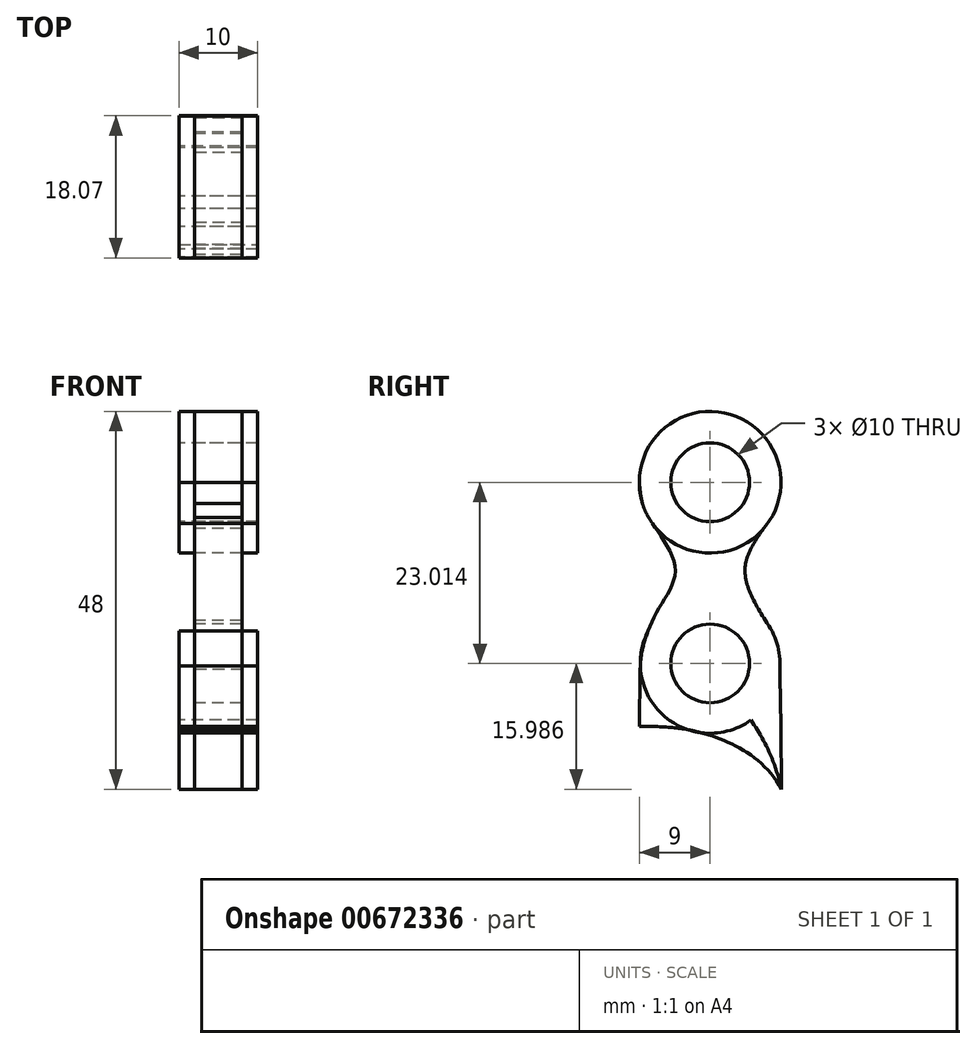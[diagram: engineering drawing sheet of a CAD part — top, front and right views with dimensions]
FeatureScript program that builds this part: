
annotation { "Feature Type Name" : "Feature", "Feature Type Description" : "" }
export const myFeature = defineFeature(function(context is Context, id is Id, definition is map)
    precondition{}
    {
        {
            var Q0;
            Q0=qCreatedBy(makeId("Right.planeOp"),FACE);
            var sketch = newSketch(context, id + "F0", { "sketchPlane" : qUnion([Q0])});
            skLineSegment(sketch, "E0.bottom", {"start": v(0, 20) * mm, "end": v(0, 20) * mm});
            skPoint(sketch, "E0.middle", {"position": v(0, 0) * mm});
            skFitSpline(sketch, "E1", {"points": [v(-9, -20) * mm, v(0, -21.15) * mm, v(9.07, -28) * mm], "startDerivative": vector(21.95, 0) * mm, "endDerivative": vector(11.4, -21.33) * mm});
            skFitSpline(sketch, "E2", {"points": [v(9.07, -28) * mm, v(9, -20) * mm], "startDerivative": vector(-0.05, 5.73) * mm, "endDerivative": vector(-0.05, 5.73) * mm});
            skPoint(sketch, "E3.visualSharp", {"position": v(9, 20) * mm});
            skArc(sketch, "E3.filletArc", {"start": v(9, 11) * mm, "mid": v(6.36, 17.36) * mm, "end": v(0, 20) * mm});
            skPoint(sketch, "E4.visualSharp", {"position": v(-9, 20) * mm});
            skArc(sketch, "E4.filletArc", {"start": v(0, 20) * mm, "mid": v(-6.36, 17.36) * mm, "end": v(-9, 11) * mm});
            skCircle(sketch, "E5", {"center": v(0, 11) * mm, "radius": 9 * mm});
            skCircle(sketch, "E6.0", {"center": v(0, 11) * mm, "radius": 5 * mm});
            skFitSpline(sketch, "E7.MirrorCS", {"points": [v(-9, -20) * mm, v(-8.54, -10) * mm, v(-6.66, -5.3) * mm, v(-4.43, 0) * mm, v(-7.33, 5.78) * mm, v(-8.59, 8.3) * mm, v(-9, 11) * mm], "startDerivative": vector(1.82, 96.63) * mm, "endDerivative": vector(-2.09, 21.27) * mm});
            skCircle(sketch, "E8", {"center": v(0, -12.01) * mm, "radius": 8.88 * mm});
            skCircle(sketch, "E9", {"center": v(0, -12.01) * mm, "radius": 5 * mm});
            skFitSpline(sketch, "E10", {"points": [v(4.43, 0) * mm, v(0, -12.01) * mm, v(9.07, -28) * mm], "startDerivative": vector(-11.72, -51.29) * mm, "endDerivative": vector(11.05, -50.26) * mm});
            skFitSpline(sketch, "E11", {"points": [v(4.43, 0) * mm, v(0, 11) * mm], "startDerivative": vector(-13.3, 18) * mm, "endDerivative": vector(-10.3, 15) * mm});
            skFitSpline(sketch, "E12", {"points": [v(7.6, 6.18) * mm, v(4.43, 0) * mm, v(7, -6.56) * mm], "startDerivative": vector(-9.2, -12.26) * mm, "endDerivative": vector(8.03, -13.2) * mm});
            skFitSpline(sketch, "E13", {"points": [v(9, -20) * mm, v(8.81, -10.96) * mm], "startDerivative": vector(-0.17, 9.05) * mm, "endDerivative": vector(-0.17, 9.05) * mm});
            skSolve(sketch);
        }
        {
            var Q0;
            {var subQ0=sQuery(id+"F0.wireOp",EDGE,"E7.MirrorCS");var subQ1=sQuery(id+"F0.wireOp",EDGE,"E1");var subQ2=makeQuery(id+"F0.imprint","INTERSECT",VERTEX,{"derivedFrom":[subQ1,subQ0]});Q0=makeQuery(id+"F0.imprint","IMPRINT",FACE,{"disambiguationData":[TD([[makeQuery(id+"F0.imprint","IMPRINT",EDGE,{"disambiguationData":[TD([[subQ2,-1.0]])],"derivedFrom":subQ1}),1.0]])]});}
            var Q1;
            {var subQ0=sQuery(id+"F0.wireOp",EDGE,"E8");var subQ1=sQuery(id+"F0.wireOp",EDGE,"E1");var subQ2=makeQuery(id+"F0.imprint","INTERSECT",VERTEX,{"disambiguationData":[OD(0.0)],"derivedFrom":[subQ1,subQ0]});Q1=makeQuery(id+"F0.imprint","IMPRINT",FACE,{"disambiguationData":[TD([[makeQuery(id+"F0.imprint","IMPRINT",EDGE,{"disambiguationData":[TD([[subQ2,-1.0]])],"derivedFrom":subQ1}),-1.0]])]});}
            var Q2;
            {var subQ0=sQuery(id+"F0.wireOp",EDGE,"E10");var subQ1=sQuery(id+"F0.wireOp",EDGE,"E1");var subQ2=makeQuery(id+"F0.imprint","INTERSECT",VERTEX,{"derivedFrom":[subQ1,subQ0]});Q2=makeQuery(id+"F0.imprint","IMPRINT",FACE,{"disambiguationData":[TD([[makeQuery(id+"F0.imprint","IMPRINT",EDGE,{"disambiguationData":[TD([[subQ2,1.0]])],"derivedFrom":subQ1}),1.0]])]});}
            var Q3;
            {var subQ0=sQuery(id+"F0.wireOp",EDGE,"E7.MirrorCS");var subQ1=sQuery(id+"F0.wireOp",EDGE,"E5");var subQ2=makeQuery(id+"F0.imprint","INTERSECT",VERTEX,{"disambiguationData":[OD(0.0)],"derivedFrom":[subQ1,subQ0]});Q3=makeQuery(id+"F0.imprint","IMPRINT",FACE,{"disambiguationData":[TD([[makeQuery(id+"F0.imprint","IMPRINT",EDGE,{"disambiguationData":[TD([[subQ2,-1.0]])],"derivedFrom":subQ1}),1.0]])]});}
            var Q4;
            {var subQ0=sQuery(id+"F0.wireOp",EDGE,"E7.MirrorCS");var subQ1=sQuery(id+"F0.wireOp",EDGE,"E5");var subQ2=makeQuery(id+"F0.imprint","INTERSECT",VERTEX,{"disambiguationData":[OD(1.0)],"derivedFrom":[subQ1,subQ0]});Q4=makeQuery(id+"F0.imprint","IMPRINT",FACE,{"disambiguationData":[TD([[makeQuery(id+"F0.imprint","IMPRINT",EDGE,{"disambiguationData":[TD([[subQ2,-1.0]])],"derivedFrom":subQ1}),-1.0]])]});}
            var Q5;
            {var subQ0=sQuery(id+"F0.wireOp",EDGE,"E7.MirrorCS");var subQ1=sQuery(id+"F0.wireOp",EDGE,"E5");var subQ2=makeQuery(id+"F0.imprint","INTERSECT",VERTEX,{"disambiguationData":[OD(2.0)],"derivedFrom":[subQ1,subQ0]});Q5=makeQuery(id+"F0.imprint","IMPRINT",FACE,{"disambiguationData":[TD([[makeQuery(id+"F0.imprint","IMPRINT",EDGE,{"disambiguationData":[TD([[subQ2,-1.0]])],"derivedFrom":subQ1}),1.0]])]});}
            var Q6;
            {var subQ0=sQuery(id+"F0.wireOp",EDGE,"E12");var subQ1=sQuery(id+"F0.wireOp",EDGE,"E5");var subQ2=makeQuery(id+"F0.imprint","INTERSECT",VERTEX,{"disambiguationData":[OD(0.0)],"derivedFrom":[subQ1,subQ0]});Q6=makeQuery(id+"F0.imprint","IMPRINT",FACE,{"disambiguationData":[TD([[makeQuery(id+"F0.imprint","IMPRINT",EDGE,{"disambiguationData":[TD([[subQ2,1.0]])],"derivedFrom":subQ1}),1.0]])]});}
            var Q7;
            {var subQ0=sQuery(id+"F0.wireOp",EDGE,"E8");var subQ1=sQuery(id+"F0.wireOp",EDGE,"E7.MirrorCS");var subQ2=makeQuery(id+"F0.imprint","INTERSECT",VERTEX,{"disambiguationData":[OD(0.0)],"derivedFrom":[subQ1,subQ0]});Q7=makeQuery(id+"F0.imprint","IMPRINT",FACE,{"disambiguationData":[TD([[makeQuery(id+"F0.imprint","IMPRINT",EDGE,{"disambiguationData":[TD([[subQ2,-1.0]])],"derivedFrom":subQ1}),1.0]])]});}
            var Q8;
            {var subQ5=sQuery(id+"F0.wireOp",EDGE,"E7.MirrorCS");var subQ7=sQuery(id+"F0.wireOp",EDGE,"E5");var subQ8=makeQuery(id+"F0.imprint","INTERSECT",VERTEX,{"disambiguationData":[OD(3.0)],"derivedFrom":[subQ7,subQ5]});Q8=makeQuery(id+"F0.imprint","IMPRINT",FACE,{"disambiguationData":[TD([[makeQuery(id+"F0.imprint","IMPRINT",EDGE,{"disambiguationData":[TD([[subQ8,-1.0]])],"derivedFrom":subQ7}),-1.0]])]});}
            extrude(context, id + "F1", {"entities" : qUnion([Q0, Q1, Q2, Q3, Q4, Q5, Q6, Q7, Q8]), "depth" : 5 * mm, "offsetDistance" : 25 * mm, "hasSecondDirection" : true, "secondDirectionOppositeDirection" : true, "secondDirectionDepth" : 5 * mm});
        }
        {
            var Q0;
            Q0 = qSketchRegion(id + "F0", true);
            extrude(context, id + "F2", {"entities" : qUnion([Q0]), "depth" : 3 * mm, "offsetDistance" : 25 * mm, "hasSecondDirection" : true, "secondDirectionOppositeDirection" : true, "secondDirectionDepth" : 3 * mm});
        }
    });
